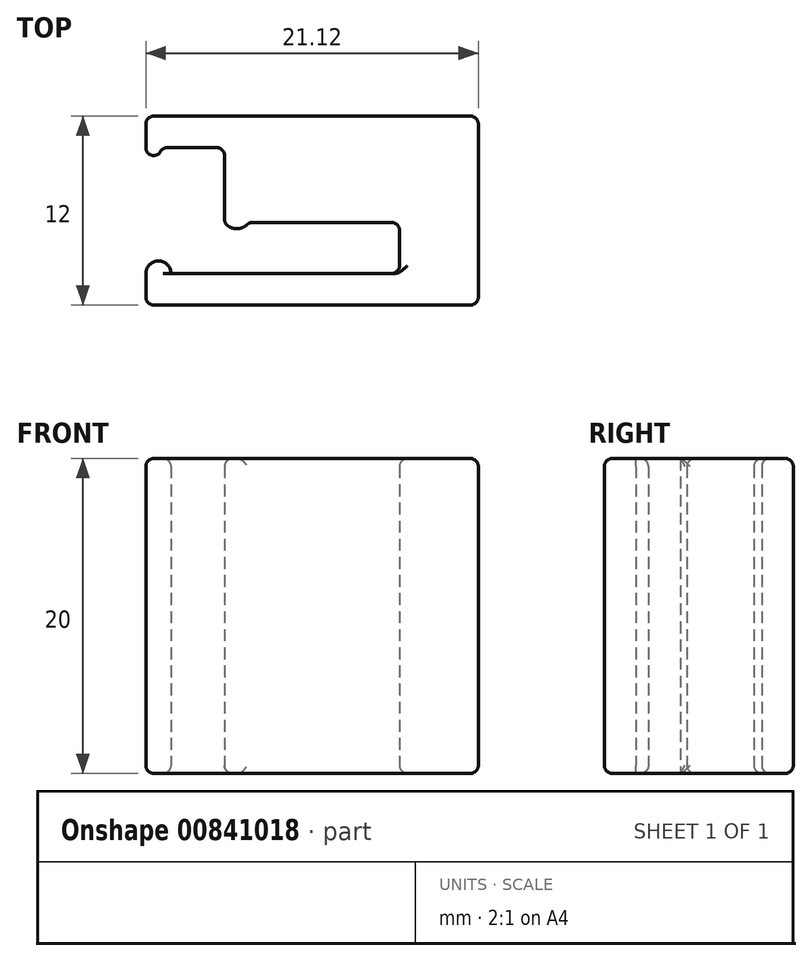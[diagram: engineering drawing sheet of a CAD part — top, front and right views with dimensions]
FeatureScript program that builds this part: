
annotation { "Feature Type Name" : "Feature", "Feature Type Description" : "" }
export const myFeature = defineFeature(function(context is Context, id is Id, definition is map)
    precondition{}
    {
        {
            var Q0;
            Q0=qCreatedBy(makeId("Top.planeOp"),FACE);
            var sketch = newSketch(context, id + "F0", { "sketchPlane" : qUnion([Q0])});
            skLineSegment(sketch, "E0", {"start": v(-25.87, -11.35) * mm, "end": v(-4.75, -11.35) * mm});
            skLineSegment(sketch, "E1", {"start": v(-9.76, -9.35) * mm, "end": v(-9.76, -6.1) * mm});
            skLineSegment(sketch, "E2", {"start": v(-9.76, -6.1) * mm, "end": v(-19.32, -6.1) * mm});
            skLineSegment(sketch, "E3", {"start": v(-20.87, -6.1) * mm, "end": v(-20.87, -1.35) * mm});
            skLineSegment(sketch, "E4", {"start": v(-20.87, -1.35) * mm, "end": v(-24.87, -1.35) * mm});
            skLineSegment(sketch, "E5", {"start": v(-25.87, 0.65) * mm, "end": v(-4.75, 0.65) * mm});
            skLineSegment(sketch, "E6", {"start": v(-4.75, 0.65) * mm, "end": v(-4.75, -11.35) * mm});
            skLineSegment(sketch, "E7", {"start": v(-25.87, 0.65) * mm, "end": v(-25.87, -1.35) * mm});
            skLineSegment(sketch, "E8", {"start": v(-25.87, -9.35) * mm, "end": v(-25.87, -11.35) * mm});
            skArc(sketch, "E9", {"start": v(-25.87, -1.35) * mm, "mid": v(-25.37, -1.85) * mm, "end": v(-24.87, -1.35) * mm});
            skArc(sketch, "E10", {"start": v(-24.27, -9.35) * mm, "mid": v(-25.07, -8.55) * mm, "end": v(-25.87, -9.35) * mm});
            skLineSegment(sketch, "E11.trimOffspring", {"start": v(-24.27, -9.35) * mm, "end": v(-9.76, -9.35) * mm});
            skArc(sketch, "E12", {"start": v(-20.87, -6.1) * mm, "mid": v(-20.1, -6.5) * mm, "end": v(-19.32, -6.1) * mm});
            skSolve(sketch);
        }
        {
            var Q0;
            Q0=makeQuery(id+"F0.imprint","IMPRINT",FACE,{"disambiguationData":[TD([[makeQuery(id+"F0.imprint","IMPRINT",EDGE,{"derivedFrom":sQuery(id+"F0.wireOp",EDGE,"E0")}),1.0]])]});
            extrude(context, id + "F1", {"entities" : qUnion([Q0]), "depth" : 20 * mm, "offsetDistance" : 25 * mm});
        }
        {
            var Q0;
            Q0=makeQuery(id+"F1.opExtrude","CAP_EDGE",EDGE,{"disambiguationData":[OSD([sQuery(id+"F0.wireOp",EDGE,"E5")])],"isStart":false});
            var Q1;
            Q1=makeQuery(id+"F1.opExtrude","SWEPT_EDGE",EDGE,{"disambiguationData":[OSD([sQuery(id+"F0.wireOp",EDGE,"E5"),sQuery(id+"F0.wireOp",EDGE,"E6")])]});
            var Q2;
            Q2=makeQuery(id+"F1.opExtrude","SWEPT_EDGE",EDGE,{"disambiguationData":[OSD([sQuery(id+"F0.wireOp",EDGE,"se2hCGv2-oCn1-JdEe-1Hst-zEXCq5JN5PH1"),sQuery(id+"F0.wireOp",EDGE,"E5")])]});
            var Q3;
            Q3=makeQuery(id+"F1.opExtrude","CAP_EDGE",EDGE,{"disambiguationData":[OSD([sQuery(id+"F0.wireOp",EDGE,"E5")])],"isStart":true});
            var Q4;
            Q4=makeQuery(id+"F1.opExtrude","CAP_EDGE",EDGE,{"disambiguationData":[OSD([sQuery(id+"F0.wireOp",EDGE,"E6")])],"isStart":false});
            var Q5;
            Q5=makeQuery(id+"F1.opExtrude","CAP_EDGE",EDGE,{"disambiguationData":[OSD([sQuery(id+"F0.wireOp",EDGE,"E6")])],"isStart":true});
            var Q6;
            Q6=makeQuery(id+"F1.opExtrude","SWEPT_EDGE",EDGE,{"disambiguationData":[OSD([sQuery(id+"F0.wireOp",EDGE,"E0"),sQuery(id+"F0.wireOp",EDGE,"E6")])]});
            var Q7;
            Q7=makeQuery(id+"F1.opExtrude","CAP_EDGE",EDGE,{"disambiguationData":[OSD([sQuery(id+"F0.wireOp",EDGE,"E0")])],"isStart":false});
            var Q8;
            Q8=makeQuery(id+"F1.opExtrude","CAP_EDGE",EDGE,{"disambiguationData":[OSD([sQuery(id+"F0.wireOp",EDGE,"E0")])],"isStart":true});
            var Q9;
            Q9=makeQuery(id+"F1.opExtrude","SWEPT_EDGE",EDGE,{"disambiguationData":[OSD([sQuery(id+"F0.wireOp",EDGE,"E0"),sQuery(id+"F0.wireOp",EDGE,"VgNkT6qo-sfCn-6F5W-kr05-qeyVZSx72ukZ")])]});
            var Q10;
            Q10=makeQuery(id+"F1.opExtrude","CAP_EDGE",EDGE,{"disambiguationData":[OSD([sQuery(id+"F0.wireOp",EDGE,"E4")])],"isStart":true});
            var Q11;
            Q11=makeQuery(id+"F1.opExtrude","CAP_EDGE",EDGE,{"disambiguationData":[OSD([sQuery(id+"F0.wireOp",EDGE,"E3")])],"isStart":true});
            var Q12;
            Q12=makeQuery(id+"F1.opExtrude","CAP_EDGE",EDGE,{"disambiguationData":[OSD([sQuery(id+"F0.wireOp",EDGE,"E2")])],"isStart":true});
            var Q13;
            Q13=makeQuery(id+"F1.opExtrude","CAP_EDGE",EDGE,{"disambiguationData":[OSD([sQuery(id+"F0.wireOp",EDGE,"E1")])],"isStart":true});
            var Q14;
            Q14=makeQuery(id+"F1.opExtrude","CAP_EDGE",EDGE,{"disambiguationData":[OSD([sQuery(id+"F0.wireOp",EDGE,"WY7y4xvH-FBVN-gxOy-u4lA-wGOGoDtsmKuX")])],"isStart":true});
            var Q15;
            Q15=makeQuery(id+"F1.opExtrude","CAP_EDGE",EDGE,{"disambiguationData":[OSD([sQuery(id+"F0.wireOp",EDGE,"E4")])],"isStart":false});
            var Q16;
            Q16=makeQuery(id+"F1.opExtrude","CAP_EDGE",EDGE,{"disambiguationData":[OSD([sQuery(id+"F0.wireOp",EDGE,"E3")])],"isStart":false});
            var Q17;
            Q17=makeQuery(id+"F1.opExtrude","CAP_EDGE",EDGE,{"disambiguationData":[OSD([sQuery(id+"F0.wireOp",EDGE,"E2")])],"isStart":false});
            var Q18;
            Q18=makeQuery(id+"F1.opExtrude","CAP_EDGE",EDGE,{"disambiguationData":[OSD([sQuery(id+"F0.wireOp",EDGE,"E1")])],"isStart":false});
            var Q19;
            Q19=makeQuery(id+"F1.opExtrude","CAP_EDGE",EDGE,{"disambiguationData":[OSD([sQuery(id+"F0.wireOp",EDGE,"WY7y4xvH-FBVN-gxOy-u4lA-wGOGoDtsmKuX")])],"isStart":false});
            var Q20;
            Q20=makeQuery(id+"F1.opExtrude","SWEPT_EDGE",EDGE,{"disambiguationData":[OSD([sQuery(id+"F0.wireOp",EDGE,"E2"),sQuery(id+"F0.wireOp",EDGE,"E3")])]});
            var Q21;
            Q21=makeQuery(id+"F1.opExtrude","SWEPT_EDGE",EDGE,{"disambiguationData":[OSD([sQuery(id+"F0.wireOp",EDGE,"VgNkT6qo-sfCn-6F5W-kr05-qeyVZSx72ukZ"),sQuery(id+"F0.wireOp",EDGE,"WY7y4xvH-FBVN-gxOy-u4lA-wGOGoDtsmKuX")])]});
            fillet(context, id + "F2", {"entities" : qUnion([Q0, Q1, Q2, Q3, Q4, Q5, Q6, Q7, Q8, Q9, Q10, Q11, Q12, Q13, Q14, Q15, Q16, Q17, Q18, Q19, Q20, Q21]), "radius" : .5 * mm, "tangentPropagation" : true, "allowEdgeOverflow" : false});
        }
        {
            var Q0;
            Q0=makeQuery(id+"F1.opExtrude","SWEPT_EDGE",EDGE,{"disambiguationData":[OSD([sQuery(id+"F0.wireOp",EDGE,"E3"),sQuery(id+"F0.wireOp",EDGE,"E4")])]});
            var Q1;
            Q1=makeQuery(id+"F1.opExtrude","SWEPT_EDGE",EDGE,{"disambiguationData":[OSD([sQuery(id+"F0.wireOp",EDGE,"E1"),sQuery(id+"F0.wireOp",EDGE,"E2")])]});
            var Q2;
            Q2=makeQuery(id+"F1.opExtrude","SWEPT_EDGE",EDGE,{"disambiguationData":[OSD([sQuery(id+"F0.wireOp",EDGE,"WY7y4xvH-FBVN-gxOy-u4lA-wGOGoDtsmKuX"),sQuery(id+"F0.wireOp",EDGE,"E1")])]});
            var Q3;
            Q3=makeQuery(id+"F1.opExtrude","SWEPT_EDGE",EDGE,{"disambiguationData":[OSD([sQuery(id+"F0.wireOp",EDGE,"E4"),sQuery(id+"F0.wireOp",EDGE,"TqxLnxR4-z3OB-T2Cr-9qos-L2ckiAXzr4NR")])]});
            fillet(context, id + "F3", {"entities" : qUnion([Q0, Q1, Q2, Q3]), "radius" : .5 * mm, "tangentPropagation" : true, "allowEdgeOverflow" : false});
        }
        {
            var Q0;
            {var subQ0=sQuery(id+"F0.wireOp",EDGE,"E9");Q0=makeQuery(id+"F0.imprint","IMPRINT",FACE,{"disambiguationData":[TD([[makeQuery(id+"F0.imprint","IMPRINT",EDGE,{"derivedFrom":subQ0}),1.0]])]});}
            var Q1;
            Q1=sQuery(id+"F0.wireOp",EDGE,"E9");
            extrude(context, id + "F4", {"entities" : qUnion([Q0]), "operationType" : NewBodyOperationType.ADD, "surfaceOperationType" : NewSurfaceOperationType.ADD, "surfaceEntities" : qUnion([Q1]), "depth" : 20 * mm, "offsetDistance" : 25 * mm});
        }
        {
            var Q0;
            Q0=makeQuery(id+"F4.opExtrude","CAP_EDGE",EDGE,{"disambiguationData":[OSD([sQuery(id+"F0.wireOp",EDGE,"E5")])],"isStart":false});
            var Q1;
            Q1=makeQuery(id+"F4.opExtrude","SWEPT_EDGE",EDGE,{"disambiguationData":[OSD([sQuery(id+"F0.wireOp",EDGE,"E5"),sQuery(id+"F0.wireOp",EDGE,"E7")])]});
            var Q2;
            Q2=makeQuery(id+"F4.opExtrude","CAP_EDGE",EDGE,{"disambiguationData":[OSD([sQuery(id+"F0.wireOp",EDGE,"E5")])],"isStart":true});
            var Q3;
            Q3=makeQuery(id+"F4.opExtrude","SWEPT_EDGE",EDGE,{"disambiguationData":[OSD([sQuery(id+"F0.wireOp",EDGE,"E5"),sQuery(id+"F0.wireOp",EDGE,"E6")])]});
            var Q4;
            Q4=makeQuery(id+"F4.opExtrude","CAP_EDGE",EDGE,{"disambiguationData":[OSD([sQuery(id+"F0.wireOp",EDGE,"E0")])],"isStart":true});
            var Q5;
            Q5=makeQuery(id+"F4.opExtrude","SWEPT_EDGE",EDGE,{"disambiguationData":[OSD([sQuery(id+"F0.wireOp",EDGE,"E0"),sQuery(id+"F0.wireOp",EDGE,"E8")])]});
            var Q6;
            Q6=makeQuery(id+"F4.opExtrude","CAP_EDGE",EDGE,{"disambiguationData":[OSD([sQuery(id+"F0.wireOp",EDGE,"E0")])],"isStart":false});
            var Q7;
            Q7=makeQuery(id+"F4.opExtrude","SWEPT_EDGE",EDGE,{"disambiguationData":[OSD([sQuery(id+"F0.wireOp",EDGE,"E0"),sQuery(id+"F0.wireOp",EDGE,"E6")])]});
            var Q8;
            Q8=makeQuery(id+"F4.opExtrude","CAP_EDGE",EDGE,{"disambiguationData":[OSD([sQuery(id+"F0.wireOp",EDGE,"E2")])],"isStart":false});
            var Q9;
            Q9=makeQuery(id+"F4.opExtrude","CAP_EDGE",EDGE,{"disambiguationData":[OSD([sQuery(id+"F0.wireOp",EDGE,"E2")])],"isStart":true});
            var Q10;
            Q10=makeQuery(id+"F4.opExtrude","SWEPT_EDGE",EDGE,{"disambiguationData":[OSD([sQuery(id+"F0.wireOp",EDGE,"E2"),sQuery(id+"F0.wireOp",EDGE,"E3")])]});
            var Q11;
            Q11=makeQuery(id+"F4.opExtrude","CAP_EDGE",EDGE,{"disambiguationData":[OSD([sQuery(id+"F0.wireOp",EDGE,"E1")])],"isStart":true});
            var Q12;
            Q12=makeQuery(id+"F4.opExtrude","CAP_EDGE",EDGE,{"disambiguationData":[OSD([sQuery(id+"F0.wireOp",EDGE,"WY7y4xvH-FBVN-gxOy-u4lA-wGOGoDtsmKuX")])],"isStart":true});
            var Q13;
            Q13=makeQuery(id+"F4.opExtrude","SWEPT_EDGE",EDGE,{"disambiguationData":[OSD([sQuery(id+"F0.wireOp",EDGE,"WY7y4xvH-FBVN-gxOy-u4lA-wGOGoDtsmKuX"),sQuery(id+"F0.wireOp",EDGE,"E8")])]});
            var Q14;
            Q14=makeQuery(id+"F4.opExtrude","CAP_EDGE",EDGE,{"disambiguationData":[OSD([sQuery(id+"F0.wireOp",EDGE,"WY7y4xvH-FBVN-gxOy-u4lA-wGOGoDtsmKuX")])],"isStart":false});
            var Q15;
            Q15=makeQuery(id+"F4.opExtrude","CAP_EDGE",EDGE,{"disambiguationData":[OSD([sQuery(id+"F0.wireOp",EDGE,"E3")])],"isStart":false});
            var Q16;
            Q16=makeQuery(id+"F4.opExtrude","CAP_EDGE",EDGE,{"disambiguationData":[OSD([sQuery(id+"F0.wireOp",EDGE,"E3")])],"isStart":true});
            var Q17;
            Q17=makeQuery(id+"F4.opExtrude","CAP_EDGE",EDGE,{"disambiguationData":[OSD([sQuery(id+"F0.wireOp",EDGE,"E6")])],"isStart":true});
            var Q18;
            Q18=makeQuery(id+"F4.opExtrude","CAP_EDGE",EDGE,{"disambiguationData":[OSD([sQuery(id+"F0.wireOp",EDGE,"E6")])],"isStart":false});
            var Q19;
            Q19=makeQuery(id+"F4.opExtrude","CAP_EDGE",EDGE,{"disambiguationData":[OSD([sQuery(id+"F0.wireOp",EDGE,"E4")])],"isStart":true});
            var Q20;
            Q20=makeQuery(id+"F4.opExtrude","CAP_EDGE",EDGE,{"disambiguationData":[OSD([sQuery(id+"F0.wireOp",EDGE,"E4")])],"isStart":false});
            var Q21;
            Q21=makeQuery(id+"F4.opExtrude","CAP_EDGE",EDGE,{"disambiguationData":[OSD([sQuery(id+"F0.wireOp",EDGE,"E1")])],"isStart":false});
            fillet(context, id + "F5", {"entities" : qUnion([Q0, Q1, Q2, Q3, Q4, Q5, Q6, Q7, Q8, Q9, Q10, Q11, Q12, Q13, Q14, Q15, Q16, Q17, Q18, Q19, Q20, Q21]), "radius" : .5 * mm, "tangentPropagation" : true, "allowEdgeOverflow" : false});
        }
        {
            var Q0;
            {var subQ0=sQuery(id+"F0.wireOp",EDGE,"E7");Q0=makeQuery(id+"F4.boolean.opBoolean","MERGE",EDGE,{"derivedFrom":[makeQuery(id+"F1.opExtrude","CAP_EDGE",EDGE,{"disambiguationData":[OSD([subQ0])],"isStart":false}),makeQuery(id+"F4.opExtrude","CAP_EDGE",EDGE,{"disambiguationData":[OSD([subQ0])],"isStart":false})]});}
            var Q1;
            {var subQ0=sQuery(id+"F0.wireOp",EDGE,"E7");Q1=makeQuery(id+"F4.boolean.opBoolean","MERGE",EDGE,{"derivedFrom":[makeQuery(id+"F1.opExtrude","CAP_EDGE",EDGE,{"disambiguationData":[OSD([subQ0])],"isStart":true}),makeQuery(id+"F4.opExtrude","CAP_EDGE",EDGE,{"disambiguationData":[OSD([subQ0])],"isStart":true})]});}
            var Q2;
            {var subQ0=sQuery(id+"F0.wireOp",EDGE,"E8");Q2=makeQuery(id+"F4.boolean.opBoolean","MERGE",EDGE,{"derivedFrom":[makeQuery(id+"F1.opExtrude","CAP_EDGE",EDGE,{"disambiguationData":[OSD([subQ0])],"isStart":false}),makeQuery(id+"F4.opExtrude","CAP_EDGE",EDGE,{"disambiguationData":[OSD([subQ0])],"isStart":false})]});}
            var Q3;
            {var subQ0=sQuery(id+"F0.wireOp",EDGE,"E8");Q3=makeQuery(id+"F4.boolean.opBoolean","MERGE",EDGE,{"derivedFrom":[makeQuery(id+"F1.opExtrude","CAP_EDGE",EDGE,{"disambiguationData":[OSD([subQ0])],"isStart":true}),makeQuery(id+"F4.opExtrude","CAP_EDGE",EDGE,{"disambiguationData":[OSD([subQ0])],"isStart":true})]});}
            fillet(context, id + "F6", {"entities" : qUnion([Q0, Q1, Q2, Q3]), "radius" : .5 * mm, "tangentPropagation" : true, "allowEdgeOverflow" : false});
        }
    });
